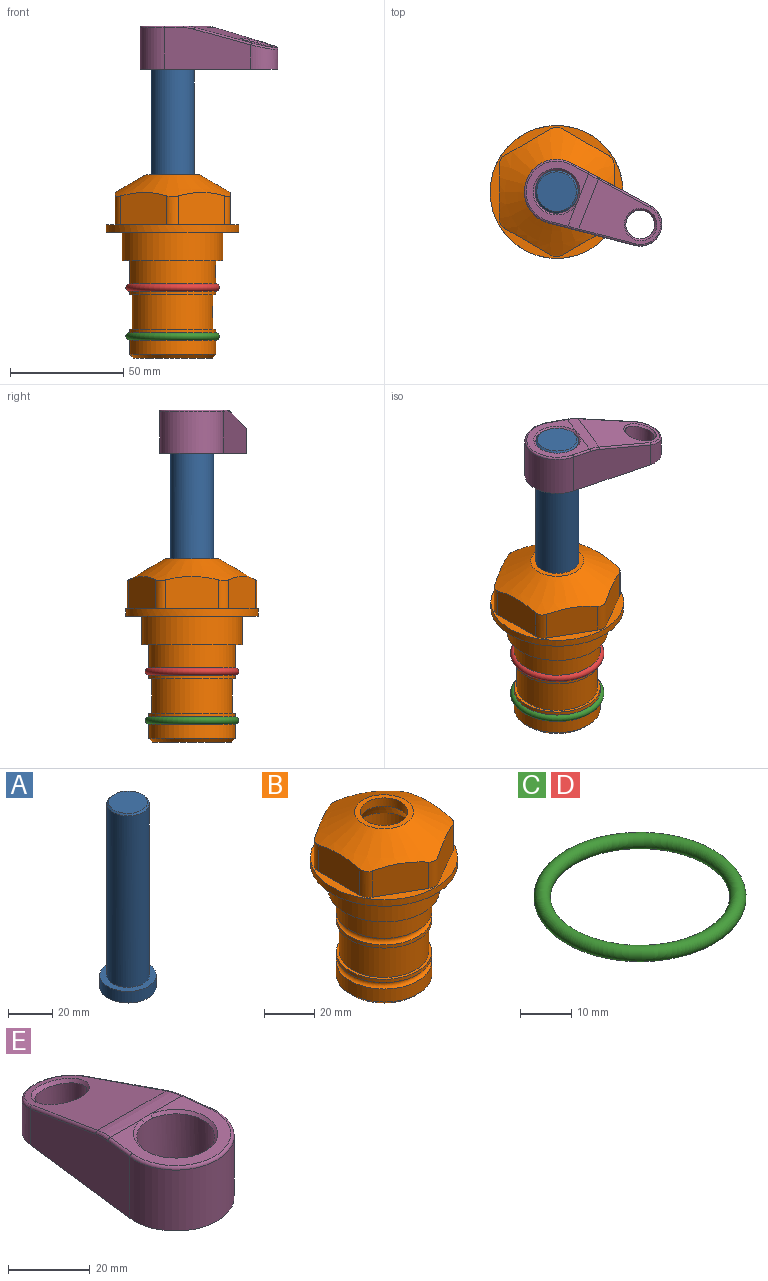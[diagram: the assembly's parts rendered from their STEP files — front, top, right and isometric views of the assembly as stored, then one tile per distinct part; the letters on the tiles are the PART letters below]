
ASSEMBLY  parts=5 mates=4
PART A: 6 faces, bbox 25.4x25.4x101.6 mm
  f0: plane 17.46x17.46mm, normal (0,0,1), area 239.5mm2, adj f5
  f1: plane 25.4x25.4mm, normal (0,0,-1), area 506.7mm2, adj f2
  f2: cylinder r=12.7mm len=25.4mm, axis (0,0,1), area 506.7mm2, adj f1,f3
  f3: plane 25.4x25.4mm, normal (0,0,1), area 221.7mm2, adj f2,f4
  f4: cylinder r=9.53mm len=94.46mm, axis (0,0,1), area 5653mm2, adj f3,f5
  f5: cone r=8.73mm half-angle=45deg, axis (0,0,-1), area 64.4mm2, adj f0,f4
PART B: 36 faces, bbox 58.7x58.7x81 mm
  f0: cylinder r=17.78mm len=35.56mm, axis (0,0,1), area 1670.8mm2, adj f23,f24,f31
  f1: cylinder r=19.05mm len=38.1mm, axis (0,0,1), area 1191.9mm2, adj f26,f27,f30
  f2: plane 58.66x58.66mm, normal (0,0,-1), area 1150.6mm2, adj f3,f28
  f3: cylinder r=29.33mm len=58.66mm, axis (0,0,-1), area 585.1mm2, adj f2,f4
  f4: plane 58.66x58.66mm, normal (0,0,1), area 475.9mm2, adj f3,f5,f6,f7,f8,f9,f10,f11
  f5: plane 20.32x14.34mm, normal (-0.5,0.87,0), area 324.4mm2, adj f4,f15,f16,f17
  f6: plane 20.32x14.34mm, normal (0.5,0.87,0), area 324.4mm2, adj f4,f14,f15,f17
  f7: plane 23.48x14.34mm, normal (1,0,0), area 324.4mm2, adj f4,f13,f14,f17
  f8: plane 20.32x14.34mm, normal (0.5,-0.87,0), area 324.4mm2, adj f4,f12,f13,f17
  f9: plane 20.32x14.34mm, normal (-0.5,-0.87,0), area 324.4mm2, adj f4,f11,f12,f17
  f10: plane 23.48x14.34mm, normal (-1,0,0), area 324.4mm2, adj f4,f11,f16,f17
  f11: cylinder r=5.08mm len=12.85mm, axis (0,0,-1), area 67.2mm2, adj f4,f9,f10,f17
  f12: cylinder r=5.08mm len=12.85mm, axis (0,0,-1), area 67.2mm2, adj f4,f8,f9,f17
  f13: cylinder r=5.08mm len=12.85mm, axis (0,0,-1), area 67.2mm2, adj f4,f7,f8,f17
  f14: cylinder r=5.08mm len=12.85mm, axis (0,0,-1), area 67.2mm2, adj f4,f6,f7,f17
  f15: cylinder r=5.08mm len=12.85mm, axis (0,0,-1), area 67.2mm2, adj f4,f5,f6,f17
  f16: cylinder r=5.08mm len=12.85mm, axis (0,0,-1), area 67.2mm2, adj f4,f5,f10,f17
  f17: cone r=11.73mm half-angle=60deg, axis (0,0,-1), area 2071.8mm2, adj f5,f6,f7,f8,f9,f10,f11,f12
  f18: plane 23.46x23.46mm, normal (0,0,1), area 147.4mm2, adj f17,f35
  f19: plane 34.93x34.93mm, normal (0,0,-1), area 958mm2, adj f29
  f20: cylinder r=19.05mm len=38.1mm, axis (0,0,1), area 760.1mm2, adj f21,f29
  f21: torus R=19.05mm, axis (0,0,1), area 565.3mm2, adj f20,f22
  f22: cylinder r=19.05mm len=38.1mm, axis (0,0,1), area 190mm2, adj f21,f23
  f23: plane 38.1x38.1mm, normal (0,0,1), area 146.9mm2, adj f0,f22
  f24: plane 38.1x38.1mm, normal (0,0,-1), area 146.9mm2, adj f0,f25
  f25: cylinder r=19.05mm len=38.1mm, axis (0,0,1), area 190mm2, adj f24,f26
  f26: torus R=19.05mm, axis (0,0,1), area 565.3mm2, adj f1,f25
  f27: plane 44.45x44.45mm, normal (0,0,-1), area 411.7mm2, adj f1,f28
  f28: cylinder r=22.23mm len=44.45mm, axis (0,0,1), area 1773.5mm2, adj f2,f27
  f29: cone r=19.05mm half-angle=45deg, axis (0,0,1), area 257.5mm2, adj f19,f20
  f30: cylinder r=3.17mm len=6.75mm, axis (-1,0,0), area 128mm2, adj f1,f33
  f31: cylinder r=3.17mm len=6.35mm, axis (-1,0,0), area 102.5mm2, adj f0,f33
  f32: plane 25.4x25.4mm, normal (0,0,1), area 506.7mm2, adj f33
  f33: cylinder r=12.7mm len=66.42mm, axis (0,0,-1), area 5236.2mm2, adj f30,f31,f32,f34
  f34: cone r=9.53mm half-angle=30deg, axis (0,0,-1), area 443.4mm2, adj f33,f35
  f35: cylinder r=9.53mm len=19.05mm, axis (0,0,-1), area 240.9mm2, adj f18,f34
PART C: 1 faces, bbox 44.7x44.7x3.2 mm
  f0: torus R=19.05mm, axis (0,0,1), area 1193.9mm2
PART D: same geometry as C
PART E: 31 faces, bbox 31.7x65.5x19.8 mm
  f0: plane 39.12x18.26mm, normal (0.99,0.12,0), area 612.2mm2, adj f1,f4,f7,f11,f13,f15
  f1: cylinder r=9.53mm len=18.91mm, axis (0,0,-1), area 296.1mm2, adj f0,f2,f7,f17
  f2: plane 39.12x18.26mm, normal (-0.99,0.12,0), area 612.2mm2, adj f1,f4,f7,f12,f14,f16
  f3: cylinder r=6.35mm len=12.7mm, axis (0,0,-1), area 362.4mm2, adj f7,f18
  f4: cylinder r=14.29mm len=28.58mm, axis (0,0,-1), area 882.2mm2, adj f0,f2,f7,f10
  f5: cylinder r=9.53mm len=19.05mm, axis (0,0,-1), area 1092.6mm2, adj f7,f19,f20
  f6: plane 26.99x23.69mm, normal (0,0,1), area 216.2mm2, adj f9,f10,f11,f12,f19
  f7: plane 63.5x28.58mm, normal (0,0,-1), area 661.8mm2, adj f0,f1,f2,f3,f4,f5,f22,f23
  f8: plane 33.52x23.6mm, normal (0,0.26,0.97), area 486mm2, adj f9,f15,f16,f17,f18
  f9: cylinder r=19.05mm len=24.72mm, axis (1,0,0), area 120.4mm2, adj f6,f8,f13,f14,f20
  f10: torus R=13.49mm, axis (0,0,1), area 59mm2, adj f4,f6,f11,f12
  f11: cylinder r=0.79mm len=8.67mm, axis (0.12,-0.99,0), area 10.8mm2, adj f0,f6,f10,f13
  f12: cylinder r=0.79mm len=8.67mm, axis (0.12,0.99,0), area 10.8mm2, adj f2,f6,f10,f14
  f13: bspline ~4.95x1.42mm, area 6.1mm2, adj f0,f9,f11,f15
  f14: bspline ~4.95x1.42mm, area 6.1mm2, adj f2,f9,f12,f16
  f15: cylinder r=0.79mm len=25.95mm, axis (0.12,-0.96,0.26), area 32.9mm2, adj f0,f8,f13,f17
  f16: cylinder r=0.79mm len=25.95mm, axis (0.12,0.96,-0.26), area 32.9mm2, adj f2,f8,f14,f17
  f17: bspline ~18.91x8.38mm, area 30mm2, adj f1,f8,f15,f16
  f18: bspline ~14.29x14.29mm, area 48.3mm2, adj f3,f8
  f19: cone r=9.53mm half-angle=45deg, axis (0,0,1), area 66.5mm2, adj f5,f6,f20
  f20: bspline ~3.22x0.96mm, area 3.5mm2, adj f5,f9,f19
  f21: plane 2.75x2.72mm, normal (0,0,-1), area 2.9mm2, adj f23,f25,f28
  f22: plane 23.05x15.88mm, normal (-0.99,-0.12,0), area 323.6mm2, adj f7,f25,f26,f27,f28,f29
  f23: plane 23.05x15.88mm, normal (0.99,-0.12,0), area 323.6mm2, adj f7,f21,f25,f27,f28,f30
  f24: cylinder r=9.53mm len=10.69mm, axis (0,0,-1), area 114.7mm2, adj f7,f27,f29,f30
  f25: cylinder r=12.7mm len=20.59mm, axis (0,0,-1), area 381.1mm2, adj f7,f21,f22,f23,f26,f28
  f26: plane 2.75x2.72mm, normal (0,0,-1), area 2.9mm2, adj f22,f25,f28
  f27: plane 19.72x18.37mm, normal (0,-0.26,-0.97), area 291.8mm2, adj f22,f23,f24,f28,f29,f30
  f28: cylinder r=15.88mm len=19.92mm, axis (1,0,0), area 54.8mm2, adj f21,f22,f23,f25,f26,f27
  f29: cylinder r=1.59mm len=11mm, axis (0,0,-1), area 34.7mm2, adj f7,f22,f24,f27
  f30: cylinder r=1.59mm len=11mm, axis (0,0,-1), area 34.7mm2, adj f7,f23,f24,f27
PLACE A rot(axis=(0,0,-1),111.4deg) t=(0,0,27.55)mm
PLACE B at identity fixed
PLACE C t=(0,0,-21.59)mm
PLACE D at identity
PLACE E rot(axis=(0,0,-1),111.4deg) t=(0,0,27.55)mm
MATE fastened E.f4 <-> A.f2  axis (0,0,1) through (0,0,91.05)mm
MATE cylindrical B.f0 <-> A.f2  axis (0,0,1) through (0,0,-50.55)mm
MATE fastened C.f0 <-> B.f0  axis (0,0,1) through (0,0,-46.1)mm
MATE fastened D.f0 <-> B.f0  axis (0,0,1) through (0,0,-24.51)mm
